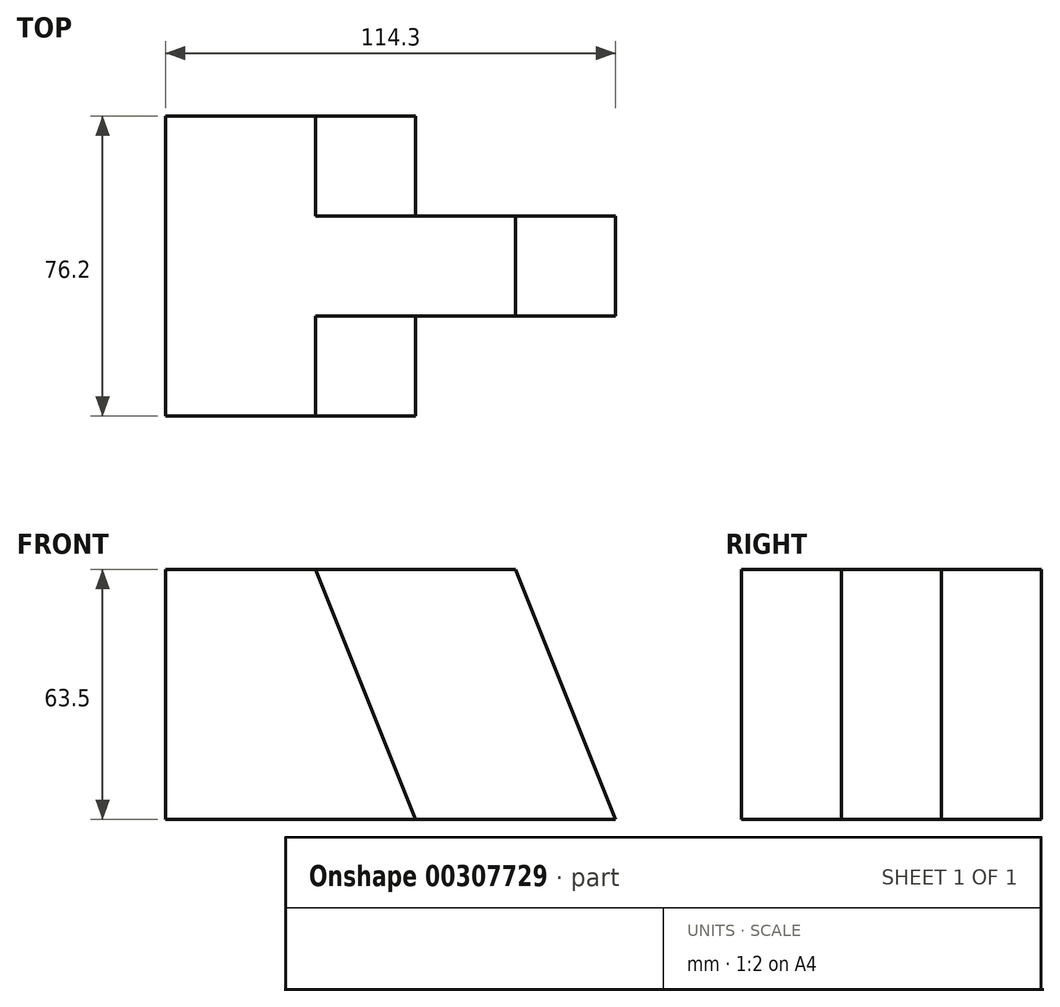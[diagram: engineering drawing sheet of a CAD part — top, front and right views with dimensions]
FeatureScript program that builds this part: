
annotation { "Feature Type Name" : "Feature", "Feature Type Description" : "" }
export const myFeature = defineFeature(function(context is Context, id is Id, definition is map)
    precondition{}
    {
        {
            var Q0;
            Q0=qCreatedBy(makeId("Top.planeOp"),FACE);
            var sketch = newSketch(context, id + "F0", { "sketchPlane" : qUnion([Q0])});
            skLineSegment(sketch, "E0", {"start": v(-37.56, -50.8) * mm, "end": v(25.94, -50.8) * mm});
            skLineSegment(sketch, "E1", {"start": v(25.94, -50.8) * mm, "end": v(25.94, -25.4) * mm});
            skLineSegment(sketch, "E2", {"start": v(25.94, -25.4) * mm, "end": v(76.74, -25.4) * mm});
            skLineSegment(sketch, "E3", {"start": v(76.74, -25.4) * mm, "end": v(76.74, 0) * mm});
            skLineSegment(sketch, "E4", {"start": v(76.74, 0) * mm, "end": v(25.94, 0) * mm});
            skLineSegment(sketch, "E5", {"start": v(25.94, 0) * mm, "end": v(25.94, 25.4) * mm});
            skLineSegment(sketch, "E6", {"start": v(25.94, 25.4) * mm, "end": v(-37.56, 25.4) * mm});
            skLineSegment(sketch, "E7", {"start": v(-37.56, 25.4) * mm, "end": v(-37.56, -50.8) * mm});
            skSolve(sketch);
        }
        {
            var Q0;
            Q0=makeQuery(id+"F0.imprint","IMPRINT",FACE,{"disambiguationData":[TD([[makeQuery(id+"F0.imprint","IMPRINT",EDGE,{"derivedFrom":sQuery(id+"F0.wireOp",EDGE,"E0")}),1.0]])]});
            extrude(context, id + "F1", {"entities" : qUnion([Q0]), "depth" : 63.5 * mm});
        }
        {
            var Q0;
            Q0=makeQuery(id+"F1.opExtrude","SWEPT_FACE",FACE,{"disambiguationData":[OSD([sQuery(id+"F0.wireOp",EDGE,"E0")])]});
            var sketch = newSketch(context, id + "F2", { "sketchPlane" : qUnion([Q0])});
            skLineSegment(sketch, "E8", {"start": v(0.54, 63.5) * mm, "end": v(25.94, 63.5) * mm});
            skLineSegment(sketch, "E9", {"start": v(25.94, 63.5) * mm, "end": v(25.94, 0) * mm});
            skLineSegment(sketch, "E10", {"start": v(25.94, 0) * mm, "end": v(0.54, 63.5) * mm});
            skSolve(sketch);
        }
        {
            var Q0;
            Q0=makeQuery(id+"F2.imprint","IMPRINT",FACE,{"disambiguationData":[TD([[makeQuery(id+"F2.imprint","IMPRINT",EDGE,{"derivedFrom":sQuery(id+"F2.wireOp",EDGE,"E8")}),-1.0]])]});
            extrude(context, id + "F3", {"entities" : qUnion([Q0]), "operationType" : NewBodyOperationType.REMOVE, "oppositeDirection" : true, "depth" : 25.4 * mm});
        }
        {
            var Q0;
            Q0=makeQuery(id+"F1.opExtrude","SWEPT_FACE",FACE,{"disambiguationData":[OSD([sQuery(id+"F0.wireOp",EDGE,"E6")])]});
            var sketch = newSketch(context, id + "F4", { "sketchPlane" : qUnion([Q0])});
            skLineSegment(sketch, "E11", {"start": v(-25.94, 63.5) * mm, "end": v(-0.54, 63.5) * mm});
            skLineSegment(sketch, "E12", {"start": v(-0.54, 63.5) * mm, "end": v(-25.94, 0) * mm});
            skLineSegment(sketch, "E13", {"start": v(-25.94, 0) * mm, "end": v(-25.94, 63.5) * mm});
            skSolve(sketch);
        }
        {
            var Q0;
            Q0=makeQuery(id+"F4.imprint","IMPRINT",FACE,{"disambiguationData":[TD([[makeQuery(id+"F4.imprint","IMPRINT",EDGE,{"derivedFrom":sQuery(id+"F4.wireOp",EDGE,"E11")}),-1.0]])]});
            extrude(context, id + "F5", {"entities" : qUnion([Q0]), "operationType" : NewBodyOperationType.REMOVE, "oppositeDirection" : true, "depth" : 25.4 * mm});
        }
        {
            var Q0;
            Q0=makeQuery(id+"F3.boolean.opBoolean","MERGE",FACE,{"derivedFrom":[makeQuery(id+"F1.opExtrude","SWEPT_FACE",FACE,{"disambiguationData":[OSD([sQuery(id+"F0.wireOp",EDGE,"E2")])]}),makeQuery(id+"F3.opExtrude","CAP_FACE",FACE,{"disambiguationData":[OSD([sQuery(id+"F2.wireOp",EDGE,"E8"),sQuery(id+"F2.wireOp",EDGE,"E9"),sQuery(id+"F2.wireOp",EDGE,"E10")])],"isStart":false})]});
            var sketch = newSketch(context, id + "F6", { "sketchPlane" : qUnion([Q0])});
            skLineSegment(sketch, "E14", {"start": v(76.74, 63.5) * mm, "end": v(51.34, 63.5) * mm});
            skLineSegment(sketch, "E15", {"start": v(51.34, 63.5) * mm, "end": v(76.74, 0) * mm});
            skLineSegment(sketch, "E16", {"start": v(76.74, 0) * mm, "end": v(76.74, 63.5) * mm});
            skSolve(sketch);
        }
        {
            var Q0;
            Q0=makeQuery(id+"F6.imprint","IMPRINT",FACE,{"disambiguationData":[TD([[makeQuery(id+"F6.imprint","IMPRINT",EDGE,{"derivedFrom":sQuery(id+"F6.wireOp",EDGE,"E14")}),-1.0]])]});
            extrude(context, id + "F7", {"entities" : qUnion([Q0]), "operationType" : NewBodyOperationType.REMOVE, "oppositeDirection" : true, "depth" : 25.4 * mm});
        }
    });
